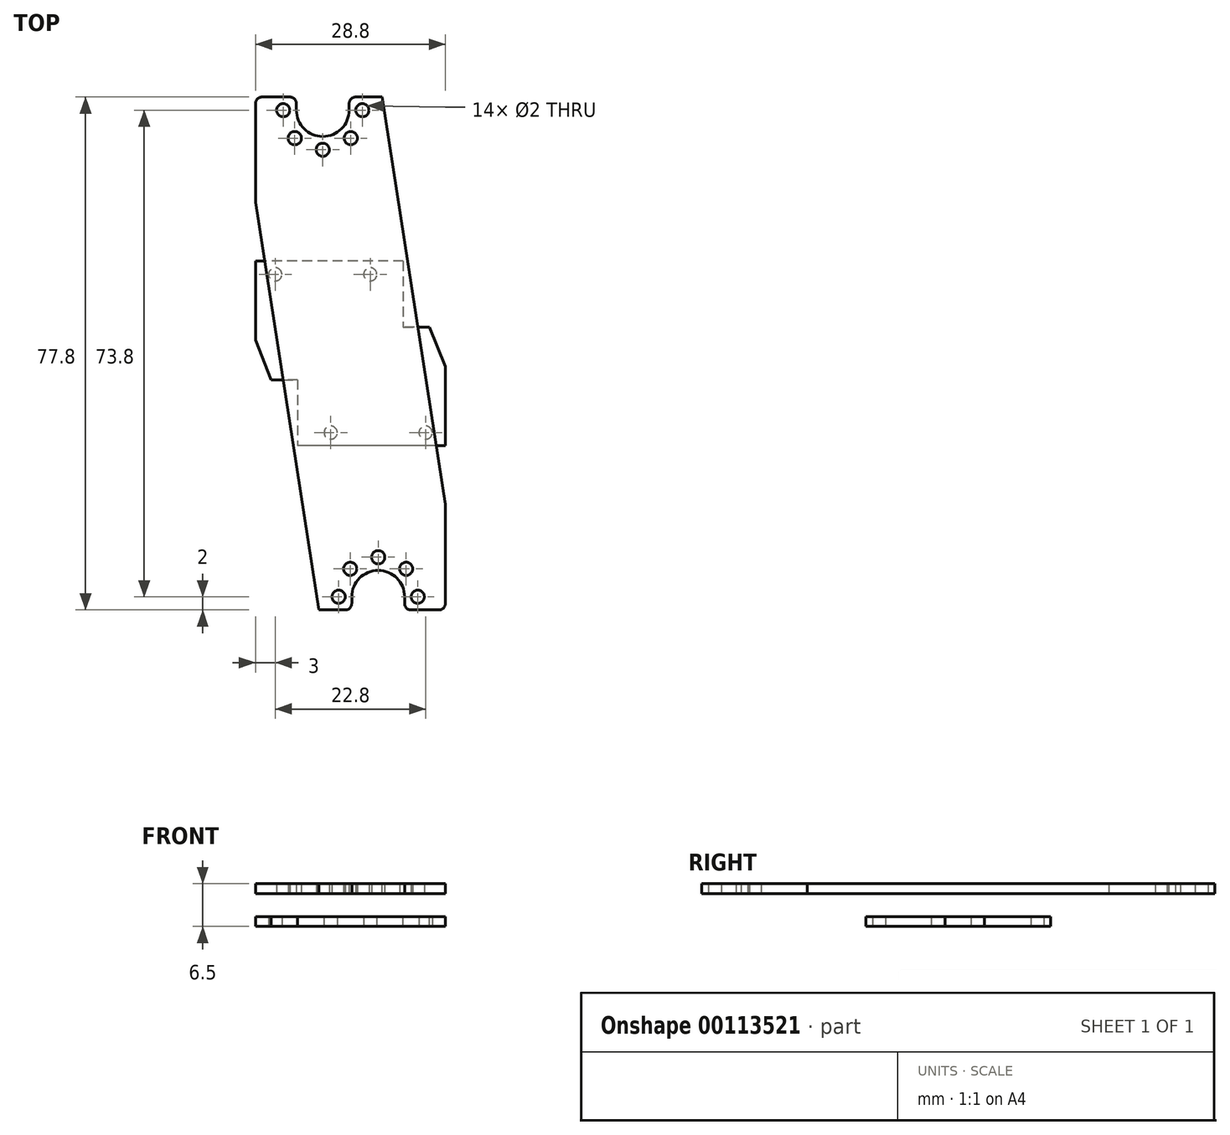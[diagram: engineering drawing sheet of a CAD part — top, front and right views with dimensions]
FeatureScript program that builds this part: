
annotation { "Feature Type Name" : "Feature", "Feature Type Description" : "" }
export const myFeature = defineFeature(function(context is Context, id is Id, definition is map)
    precondition{}
    {
        {
            var Q0;
            Q0=qCreatedBy(makeId("Top.planeOp"),FACE);
            var sketch = newSketch(context, id + "F0", { "sketchPlane" : qUnion([Q0])});
            skLineSegment(sketch, "E0.bottom", {"start": v(14.4, -14) * mm, "end": v(-14.4, -14) * mm});
            skLineSegment(sketch, "E0.top", {"start": v(14.4, 14) * mm, "end": v(-14.4, 14) * mm});
            skLineSegment(sketch, "E0.left", {"start": v(14.4, -14) * mm, "end": v(14.4, 14) * mm});
            skLineSegment(sketch, "E0.right", {"start": v(-14.4, -14) * mm, "end": v(-14.4, 14) * mm});
            skPoint(sketch, "E0.middle", {"position": v(0, 0) * mm});
            skCircle(sketch, "E1", {"center": v(-11.4, 12) * mm, "radius": 1 * mm});
            skCircle(sketch, "E2", {"center": v(3, 12) * mm, "radius": 1 * mm});
            skCircle(sketch, "E3", {"center": v(-4.2, 36.9) * mm, "radius": 6 * mm, "construction": true});
            skLineSegment(sketch, "E4", {"start": v(-11.4, 12) * mm, "end": v(3, 12) * mm, "construction": true});
            skPoint(sketch, "E5", {"position": v(-4.2, 12) * mm});
            skCircle(sketch, "E6.MirrorC", {"center": v(11.4, 12) * mm, "radius": 1 * mm, "construction": true});
            skCircle(sketch, "E7.MirrorC", {"center": v(-3, 12) * mm, "radius": 1 * mm, "construction": true});
            skCircle(sketch, "E8.MirrorC", {"center": v(-3, -12) * mm, "radius": 1 * mm});
            skCircle(sketch, "E9.MirrorC", {"center": v(11.4, -12) * mm, "radius": 1 * mm});
            skSolve(sketch);
        }
        {
            var Q0;
            Q0=qSketchRegion(id+"F0",true);
            extrude(context, id + "F1", {"entities" : qUnion([Q0]), "depth" : 1.5 * mm});
        }
        {
            var Q0;
            Q0=makeQuery(id+"F1.opExtrude","CAP_FACE",FACE,{"disambiguationData":[OSD([sQuery(id+"F0.wireOp",EDGE,"E0.bottom"),sQuery(id+"F0.wireOp",EDGE,"E0.top"),sQuery(id+"F0.wireOp",EDGE,"E0.left"),sQuery(id+"F0.wireOp",EDGE,"E0.right"),sQuery(id+"F0.wireOp",EDGE,"E1"),sQuery(id+"F0.wireOp",EDGE,"E2"),sQuery(id+"F0.wireOp",EDGE,"E8.MirrorC"),sQuery(id+"F0.wireOp",EDGE,"E9.MirrorC")])],"isStart":false});
            var sketch = newSketch(context, id + "F2", { "sketchPlane" : qUnion([Q0])});
            skPoint(sketch, "E10", {"position": v(-11.4, 12) * mm});
            skPoint(sketch, "E11", {"position": v(3, 12) * mm});
            skPoint(sketch, "E12", {"position": v(-3, -12) * mm});
            skPoint(sketch, "E13", {"position": v(11.4, -12) * mm});
            skLineSegment(sketch, "E14", {"start": v(-14.4, 2) * mm, "end": v(-12, -4) * mm});
            skLineSegment(sketch, "E15", {"start": v(-8, -14) * mm, "end": v(-14.4, -14) * mm});
            skLineSegment(sketch, "E16", {"start": v(-14.4, -14) * mm, "end": v(-14.4, 2) * mm});
            skLineSegment(sketch, "E17.MirrorCS", {"start": v(14.4, 2) * mm, "end": v(8, -14) * mm, "construction": true});
            skLineSegment(sketch, "E18.MirrorCS", {"start": v(14.4, -14) * mm, "end": v(14.4, 2) * mm, "construction": true});
            skLineSegment(sketch, "E19.MirrorCS", {"start": v(8, -14) * mm, "end": v(14.4, -14) * mm, "construction": true});
            skLineSegment(sketch, "E20.MirrorCS", {"start": v(12, 4) * mm, "end": v(10.4, 8) * mm});
            skLineSegment(sketch, "E21.MirrorCS", {"start": v(14.4, 14) * mm, "end": v(14.4, -2) * mm});
            skLineSegment(sketch, "E22.MirrorCS", {"start": v(8, 14) * mm, "end": v(14.4, 14) * mm});
            skLineSegment(sketch, "E23", {"start": v(8, 14) * mm, "end": v(8, 4) * mm});
            skLineSegment(sketch, "E24", {"start": v(8, 4) * mm, "end": v(12, 4) * mm});
            skLineSegment(sketch, "E25", {"start": v(10.4, 8) * mm, "end": v(10.4, -2) * mm, "construction": true});
            skLineSegment(sketch, "E26", {"start": v(10.4, -2) * mm, "end": v(14.4, -2) * mm, "construction": true});
            skLineSegment(sketch, "E27", {"start": v(10.4, 8) * mm, "end": v(14.4, -2) * mm});
            skLineSegment(sketch, "E28", {"start": v(-12, -4) * mm, "end": v(-8, -4) * mm});
            skLineSegment(sketch, "E29", {"start": v(-8, -4) * mm, "end": v(-8, -14) * mm});
            skSolve(sketch);
        }
        {
            var Q0;
            Q0=qSketchRegion(id+"F2",true);
            extrude(context, id + "F3", {"entities" : qUnion([Q0]), "operationType" : NewBodyOperationType.REMOVE, "endBound" : BoundingType.UP_TO_NEXT, "oppositeDirection" : true, "depth" : 25 * mm});
        }
        {
            var Q0;
            Q0=qCreatedBy(makeId("Top.planeOp"),FACE);
            cPlane(context, id + "F4", {"entities" : qUnion([Q0]), "cplaneType" : CPlaneType.OFFSET, "offset" : 5 * mm, "width" : 150 * mm, "height" : 150 * mm});
        }
        {
            var Q0;
            Q0=qCreatedBy(id+"F4.planeOp",FACE);
            var sketch = newSketch(context, id + "F5", { "sketchPlane" : qUnion([Q0])});
            skLineSegment(sketch, "E30.bottom", {"start": v(-14.4, 38.9) * mm, "end": v(-8.2, 38.9) * mm});
            skLineSegment(sketch, "E30.top", {"start": v(-14.4, -38.9) * mm, "end": v(0.2, -38.9) * mm});
            skLineSegment(sketch, "E30.left", {"start": v(-14.4, 38.9) * mm, "end": v(-14.4, -38.9) * mm});
            skLineSegment(sketch, "E30.right", {"start": v(14.4, 38.9) * mm, "end": v(14.4, -38.9) * mm});
            skPoint(sketch, "E30.middle", {"position": v(0, 0) * mm});
            skLineSegment(sketch, "E31.0", {"start": v(-14.4, -14) * mm, "end": v(-14.4, 14) * mm, "construction": true});
            skLineSegment(sketch, "E32.0", {"start": v(14.4, -14) * mm, "end": v(14.4, 14) * mm, "construction": true});
            skCircle(sketch, "E33.0", {"center": v(-4.2, 36.9) * mm, "radius": 6 * mm, "construction": true});
            skArc(sketch, "E34", {"start": v(-8.2, 36.9) * mm, "mid": v(-4.2, 32.9) * mm, "end": v(-0.2, 36.9) * mm});
            skCircle(sketch, "E35", {"center": v(-4.2, 30.9) * mm, "radius": 1 * mm});
            skCircle(sketch, "E36.1.0", {"center": v(0.04, 32.66) * mm, "radius": 1 * mm});
            skCircle(sketch, "E36.2.0", {"center": v(1.8, 36.9) * mm, "radius": 1 * mm});
            skCircle(sketch, "E36.6.0", {"center": v(-10.2, 36.9) * mm, "radius": 1 * mm});
            skCircle(sketch, "E36.7.0", {"center": v(-8.44, 32.66) * mm, "radius": 1 * mm});
            skLineSegment(sketch, "E37", {"start": v(-8.2, 36.9) * mm, "end": v(-8.2, 38.9) * mm});
            skLineSegment(sketch, "E38", {"start": v(-0.2, 36.9) * mm, "end": v(-0.2, 38.9) * mm});
            skLineSegment(sketch, "E39.trimOffspring", {"start": v(-0.2, 38.9) * mm, "end": v(14.4, 38.9) * mm});
            skLineSegment(sketch, "E40.MirrorCS", {"start": v(8.2, 36.9) * mm, "end": v(8.2, 38.9) * mm, "construction": true});
            skLineSegment(sketch, "E41.MirrorCS", {"start": v(0.2, 36.9) * mm, "end": v(0.2, 38.9) * mm, "construction": true});
            skArc(sketch, "E42.MirrorCS", {"start": v(8.2, 36.9) * mm, "mid": v(4.2, 32.9) * mm, "end": v(0.2, 36.9) * mm, "construction": true});
            skCircle(sketch, "E43.MirrorC", {"center": v(-1.8, 36.9) * mm, "radius": 1 * mm, "construction": true});
            skCircle(sketch, "E44.MirrorC", {"center": v(-0.04, 32.66) * mm, "radius": 1 * mm, "construction": true});
            skCircle(sketch, "E45.MirrorC", {"center": v(4.2, 30.9) * mm, "radius": 1 * mm, "construction": true});
            skCircle(sketch, "E46.MirrorC", {"center": v(8.44, 32.66) * mm, "radius": 1 * mm, "construction": true});
            skCircle(sketch, "E47.MirrorC", {"center": v(10.2, 36.9) * mm, "radius": 1 * mm, "construction": true});
            skLineSegment(sketch, "E48.MirrorCS", {"start": v(0.2, -36.9) * mm, "end": v(0.2, -38.9) * mm});
            skLineSegment(sketch, "E49.MirrorCS", {"start": v(8.2, -36.9) * mm, "end": v(8.2, -38.9) * mm});
            skArc(sketch, "E50.MirrorCS", {"start": v(8.2, -36.9) * mm, "mid": v(4.2, -32.9) * mm, "end": v(0.2, -36.9) * mm});
            skCircle(sketch, "E51.MirrorC", {"center": v(-0.04, -32.66) * mm, "radius": 1 * mm});
            skCircle(sketch, "E52.MirrorC", {"center": v(8.44, -32.66) * mm, "radius": 1 * mm});
            skCircle(sketch, "E53.MirrorC", {"center": v(10.2, -36.9) * mm, "radius": 1 * mm});
            skCircle(sketch, "E54.MirrorC", {"center": v(4.2, -30.9) * mm, "radius": 1 * mm});
            skCircle(sketch, "E55.MirrorC", {"center": v(-1.8, -36.9) * mm, "radius": 1 * mm});
            skLineSegment(sketch, "E56.trimOffspring", {"start": v(8.2, -38.9) * mm, "end": v(14.4, -38.9) * mm});
            skSolve(sketch);
        }
        {
            var Q0;
            Q0=qSketchRegion(id+"F5",true);
            extrude(context, id + "F6", {"entities" : qUnion([Q0]), "depth" : 1.5 * mm});
        }
        {
            var Q0;
            Q0=makeQuery(id+"F6.opExtrude","CAP_FACE",FACE,{"disambiguationData":[OSD([sQuery(id+"F5.wireOp",EDGE,"E30.bottom"),sQuery(id+"F5.wireOp",EDGE,"E30.top"),sQuery(id+"F5.wireOp",EDGE,"E30.left"),sQuery(id+"F5.wireOp",EDGE,"E30.right"),sQuery(id+"F5.wireOp",EDGE,"E34"),sQuery(id+"F5.wireOp",EDGE,"E35"),sQuery(id+"F5.wireOp",EDGE,"E36.1.0"),sQuery(id+"F5.wireOp",EDGE,"E36.2.0"),sQuery(id+"F5.wireOp",EDGE,"E36.6.0"),sQuery(id+"F5.wireOp",EDGE,"E36.7.0"),sQuery(id+"F5.wireOp",EDGE,"E37"),sQuery(id+"F5.wireOp",EDGE,"E38"),sQuery(id+"F5.wireOp",EDGE,"E39.trimOffspring"),sQuery(id+"F5.wireOp",EDGE,"E48.MirrorCS"),sQuery(id+"F5.wireOp",EDGE,"E49.MirrorCS"),sQuery(id+"F5.wireOp",EDGE,"E50.MirrorCS"),sQuery(id+"F5.wireOp",EDGE,"E51.MirrorC"),sQuery(id+"F5.wireOp",EDGE,"E52.MirrorC"),sQuery(id+"F5.wireOp",EDGE,"E53.MirrorC"),sQuery(id+"F5.wireOp",EDGE,"E54.MirrorC"),sQuery(id+"F5.wireOp",EDGE,"E55.MirrorC"),sQuery(id+"F5.wireOp",EDGE,"E56.trimOffspring")])],"isStart":false});
            var sketch = newSketch(context, id + "F7", { "sketchPlane" : qUnion([Q0])});
            skPoint(sketch, "E57", {"position": v(-4.2, 30.9) * mm});
            skPoint(sketch, "E58", {"position": v(-1.8, -36.9) * mm});
            skPoint(sketch, "E59", {"position": v(4.2, -30.9) * mm});
            skPoint(sketch, "E60", {"position": v(1.8, 36.9) * mm});
            skLineSegment(sketch, "E61", {"start": v(-14.4, 22.9) * mm, "end": v(-4.8, -38.9) * mm});
            skLineSegment(sketch, "E62", {"start": v(-4.8, -38.9) * mm, "end": v(-14.4, -38.9) * mm});
            skLineSegment(sketch, "E63", {"start": v(-14.4, -38.9) * mm, "end": v(-14.4, 22.9) * mm});
            skLineSegment(sketch, "E64.MirrorCS", {"start": v(14.4, -38.9) * mm, "end": v(14.4, 22.9) * mm, "construction": true});
            skLineSegment(sketch, "E65.MirrorCS", {"start": v(14.4, 22.9) * mm, "end": v(4.8, -38.9) * mm, "construction": true});
            skLineSegment(sketch, "E66.MirrorCS", {"start": v(4.8, -38.9) * mm, "end": v(14.4, -38.9) * mm, "construction": true});
            skLineSegment(sketch, "E67.MirrorCS", {"start": v(14.4, -22.9) * mm, "end": v(4.8, 38.9) * mm});
            skLineSegment(sketch, "E68.MirrorCS", {"start": v(14.4, 38.9) * mm, "end": v(14.4, -22.9) * mm});
            skLineSegment(sketch, "E69.MirrorCS", {"start": v(4.8, 38.9) * mm, "end": v(14.4, 38.9) * mm});
            skSolve(sketch);
        }
        {
            var Q0;
            Q0=qSketchRegion(id+"F7",true);
            extrude(context, id + "F8", {"entities" : qUnion([Q0]), "operationType" : NewBodyOperationType.REMOVE, "endBound" : BoundingType.UP_TO_NEXT, "oppositeDirection" : true, "depth" : 25 * mm});
        }
        {
            var Q0;
            Q0=makeQuery(id+"F8.boolean.opBoolean","COPY",EDGE,{"derivedFrom":makeQuery(id+"F8.opExtrude","SWEPT_EDGE",EDGE,{"disambiguationData":[OSD([sQuery(id+"F5.wireOp",EDGE,"E30.top"),sQuery(id+"F7.wireOp",EDGE,"E61"),sQuery(id+"F7.wireOp",EDGE,"E62")])]})});
            var Q1;
            Q1=makeQuery(id+"F6.opExtrude","SWEPT_EDGE",EDGE,{"disambiguationData":[OSD([sQuery(id+"F5.wireOp",EDGE,"E30.top"),sQuery(id+"F5.wireOp",EDGE,"E48.MirrorCS")])]});
            var Q2;
            Q2=makeQuery(id+"F6.opExtrude","SWEPT_EDGE",EDGE,{"disambiguationData":[OSD([sQuery(id+"F5.wireOp",EDGE,"E49.MirrorCS"),sQuery(id+"F5.wireOp",EDGE,"E56.trimOffspring")])]});
            var Q3;
            Q3=makeQuery(id+"F6.opExtrude","SWEPT_EDGE",EDGE,{"disambiguationData":[OSD([sQuery(id+"F5.wireOp",EDGE,"E30.right"),sQuery(id+"F5.wireOp",EDGE,"E56.trimOffspring")])]});
            var Q4;
            Q4=makeQuery(id+"F8.boolean.opBoolean","COPY",EDGE,{"derivedFrom":makeQuery(id+"F8.opExtrude","SWEPT_EDGE",EDGE,{"disambiguationData":[OSD([sQuery(id+"F5.wireOp",EDGE,"E39.trimOffspring"),sQuery(id+"F7.wireOp",EDGE,"E67.MirrorCS"),sQuery(id+"F7.wireOp",EDGE,"E69.MirrorCS")])]})});
            var Q5;
            Q5=makeQuery(id+"F6.opExtrude","SWEPT_EDGE",EDGE,{"disambiguationData":[OSD([sQuery(id+"F5.wireOp",EDGE,"E38"),sQuery(id+"F5.wireOp",EDGE,"E39.trimOffspring")])]});
            var Q6;
            Q6=makeQuery(id+"F6.opExtrude","SWEPT_EDGE",EDGE,{"disambiguationData":[OSD([sQuery(id+"F5.wireOp",EDGE,"E30.bottom"),sQuery(id+"F5.wireOp",EDGE,"E37")])]});
            var Q7;
            Q7=makeQuery(id+"F6.opExtrude","SWEPT_EDGE",EDGE,{"disambiguationData":[OSD([sQuery(id+"F5.wireOp",EDGE,"E30.bottom"),sQuery(id+"F5.wireOp",EDGE,"E30.left")])]});
            fillet(context, id + "F9", {"entities" : qUnion([Q0, Q1, Q2, Q3, Q4, Q5, Q6, Q7]), "radius" : 1 * mm, "tangentPropagation" : true, "allowEdgeOverflow" : false});
        }
    });
